# Revit family: STH20915BR_STH20915PTO
name_source: partatom
category: Luminárias
units: mm (PartAtom-declared; Revit-internal decimal feet)

## family parameters
Compartilhado = Não
Corte com vazios quando carregada = Não
Cota do conector redondo = Utilizar diâmetro
Fonte luminosa = Não
Hospedeiro = Forro
Manter orientação da anotação = Não
Número OmniClass = 23.80.70.11
Ponto de cálculo do ambiente = Não
Sempre na vertical = Sim
Tipo de parte = Normal
Título OmniClass = Luminaries for Internal Lighting

## types (2) — shared parameters
Altura = 0.12 m
Comentários de tipos = Lâmpada indicada: 1x MR16 GU10 Stella.
Comprimento = 0.1 m
Fabricante = Stella
Grau de proteção (IP) = IP20
Largura = 0.1 m
Modelo = Square Out MR16
Potência máxima = 15 W
Tensão Elétrica = 127V-220V
URL = https://stella.com.br
zero-valued in all types: Elevação padrão

## per-type parameters (varying)
| type | Base Fixação Branca | Base Fixação Preta | Estrutura | Flange Branca | Flange Preta | Plafon Branco | Plafon Preto | Referência |
| STH20915PTO - BIVOLT | Não | Sim | Al - Preto | Não | Sim | Não | Sim | STH20915PTO |
| STH20915BR - BIVOLT | Sim | Não | Al - Branco | Sim | Não | Sim | Não | STH20915BR |
